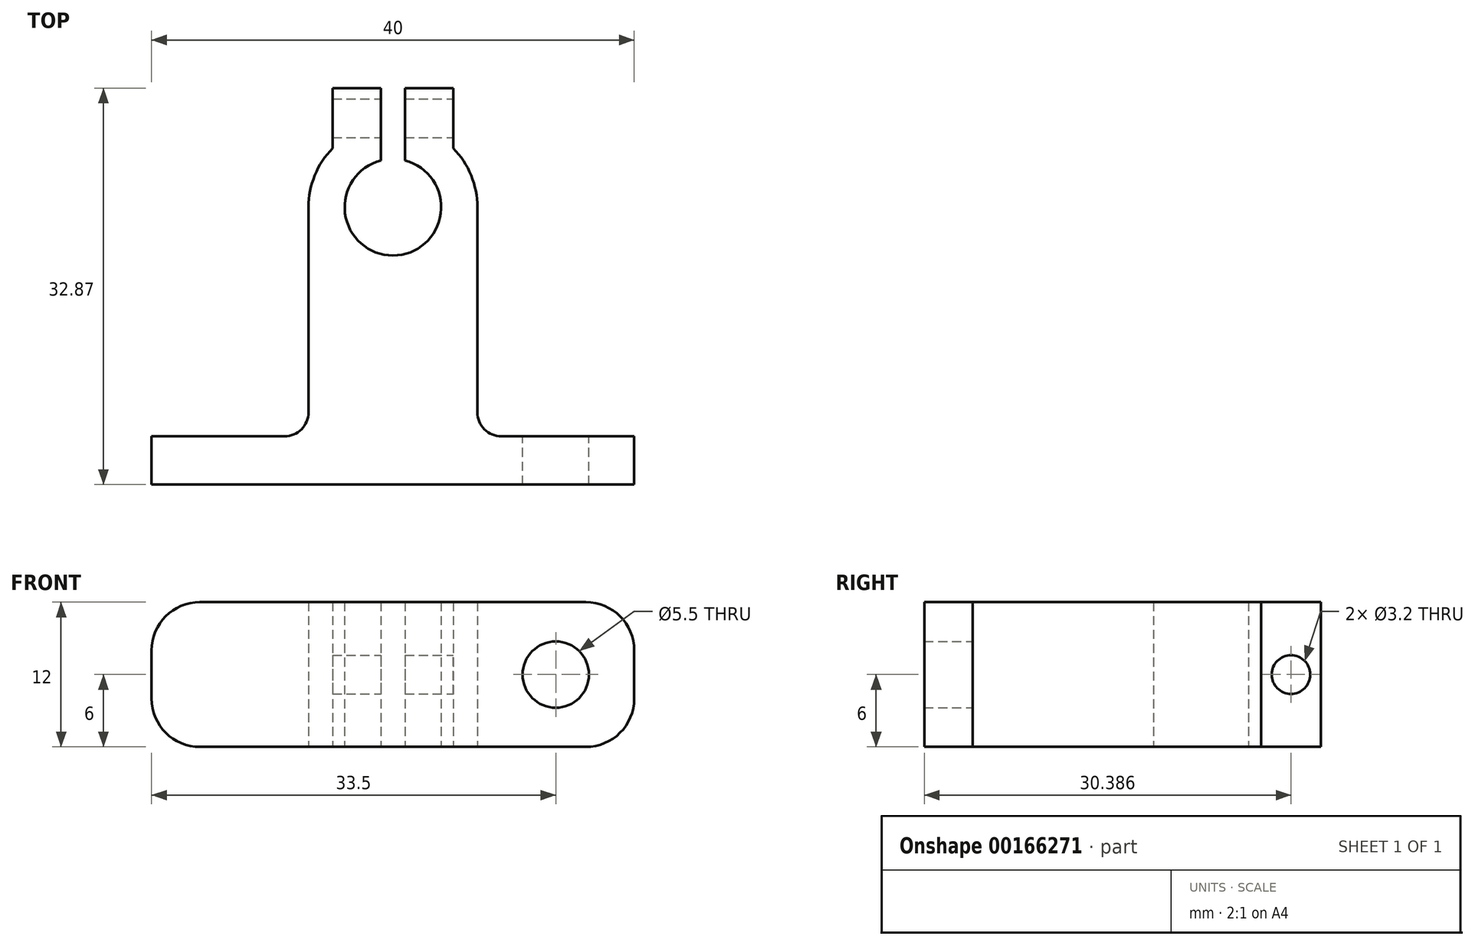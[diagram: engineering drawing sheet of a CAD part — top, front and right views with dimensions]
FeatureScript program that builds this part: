
annotation { "Feature Type Name" : "Feature", "Feature Type Description" : "" }
export const myFeature = defineFeature(function(context is Context, id is Id, definition is map)
    precondition{}
    {
        {
            var Q0;
            Q0=qCreatedBy(makeId("Top.planeOp"),FACE);
            var sketch = newSketch(context, id + "F0", { "sketchPlane" : qUnion([Q0])});
            skArc(sketch, "E0", {"start": v(-1, 3.87) * mm, "mid": v(0, -4) * mm, "end": v(1, 3.87) * mm});
            skArc(sketch, "E1.0", {"start": v(-5, 4.9) * mm, "mid": v(-6.48, 2.65) * mm, "end": v(-7, 0) * mm});
            skLineSegment(sketch, "E2", {"start": v(7, 0) * mm, "end": v(7, -19) * mm});
            skLineSegment(sketch, "E3", {"start": v(7, -19) * mm, "end": v(20, -19) * mm});
            skLineSegment(sketch, "E4", {"start": v(20, -19) * mm, "end": v(20, -23) * mm});
            skLineSegment(sketch, "E5", {"start": v(20, -23) * mm, "end": v(0, -23) * mm});
            skLineSegment(sketch, "E6", {"start": v(0, 0) * mm, "end": v(0, -23) * mm, "construction": true});
            skLineSegment(sketch, "E7", {"start": v(0, 0) * mm, "end": v(0, 4) * mm, "construction": true});
            skLineSegment(sketch, "E8.0", {"start": v(1, 3.87) * mm, "end": v(1, 6.87) * mm});
            skLineSegment(sketch, "E9.0", {"start": v(-1, 3.87) * mm, "end": v(-1, 6.93) * mm});
            skLineSegment(sketch, "E10.MirrorCS", {"start": v(-7, -19) * mm, "end": v(-20, -19) * mm});
            skLineSegment(sketch, "E11.MirrorCS", {"start": v(-20, -19) * mm, "end": v(-20, -23) * mm});
            skArc(sketch, "E12.MirrorCS", {"start": v(1, 3.87) * mm, "mid": v(0, -4) * mm, "end": v(-1, 3.87) * mm});
            skLineSegment(sketch, "E13.MirrorCS", {"start": v(-7, 0) * mm, "end": v(-7, -19) * mm});
            skLineSegment(sketch, "E14.MirrorCS", {"start": v(-20, -23) * mm, "end": v(0, -23) * mm});
            skLineSegment(sketch, "E15.top", {"start": v(-5, 9.87) * mm, "end": v(-1, 9.87) * mm});
            skLineSegment(sketch, "E15.left", {"start": v(-5, 4.9) * mm, "end": v(-5, 9.87) * mm});
            skLineSegment(sketch, "E15.right", {"start": v(-1, 3.87) * mm, "end": v(-1, 9.87) * mm});
            skLineSegment(sketch, "E16.MirrorCS", {"start": v(1, 3.87) * mm, "end": v(1, 9.87) * mm});
            skLineSegment(sketch, "E17.MirrorCS", {"start": v(5, 9.87) * mm, "end": v(1, 9.87) * mm});
            skLineSegment(sketch, "E18.MirrorCS", {"start": v(5, 4.9) * mm, "end": v(5, 9.87) * mm});
            skArc(sketch, "E19.MirrorCS", {"start": v(5, 4.9) * mm, "mid": v(6.48, 2.65) * mm, "end": v(7, 0) * mm});
            skSolve(sketch);
        }
        {
            var Q0;
            Q0=makeQuery(id+"F0.imprint","IMPRINT",FACE,{"disambiguationData":[TD([[makeQuery(id+"F0.imprint","IMPRINT",EDGE,{"derivedFrom":sQuery(id+"F0.wireOp",EDGE,"E1.0")}),1.0]])]});
            extrude(context, id + "F1", {"entities" : qUnion([Q0]), "depth" : 12 * mm});
        }
        {
            var Q0;
            Q0=makeQuery(id+"F1.opExtrude","SWEPT_FACE",FACE,{"disambiguationData":[OSD([sQuery(id+"F0.wireOp",EDGE,"E3")])]});
            var sketch = newSketch(context, id + "F2", { "sketchPlane" : qUnion([Q0])});
            skCircle(sketch, "E20", {"center": v(-13.5, 6) * mm, "radius": 2.75 * mm});
            skPoint(sketch, "E20.centerSnap0", {"position": v(-20, 6) * mm});
            skPoint(sketch, "E20.centerSnap1", {"position": v(-13.5, 0) * mm});
            skLineSegment(sketch, "E21", {"start": v(-20, 0) * mm, "end": v(20, 0) * mm, "construction": true});
            skLineSegment(sketch, "E22", {"start": v(0, 0) * mm, "end": v(0, 12) * mm, "construction": true});
            skPoint(sketch, "E22.endSnap0", {"position": v(0, 0) * mm});
            skCircle(sketch, "E23.MirrorC", {"center": v(13.5, 6) * mm, "radius": 2.75 * mm});
            skSolve(sketch);
        }
        {
            var Q0;
            Q0=makeQuery(id+"F2.imprint","IMPRINT",FACE,{"disambiguationData":[TD([[makeQuery(id+"F2.imprint","IMPRINT",EDGE,{"derivedFrom":sQuery(id+"F2.wireOp",EDGE,"E20")}),1.0]])]});
            var Q1;
            Q1=makeQuery(id+"F2.imprint","IMPRINT",FACE,{"disambiguationData":[TD([[makeQuery(id+"F2.imprint","IMPRINT",EDGE,{"derivedFrom":sQuery(id+"F2.wireOp",EDGE,"E23.MirrorC")}),-1.0]])]});
            extrude(context, id + "F3", {"entities" : qUnion([Q0, Q1]), "operationType" : NewBodyOperationType.REMOVE, "oppositeDirection" : true, "depth" : 25 * mm});
        }
        {
            var Q0;
            Q0=makeQuery(id+"F1.opExtrude","CAP_EDGE",EDGE,{"disambiguationData":[OSD([sQuery(id+"F0.wireOp",EDGE,"E4")])],"isStart":false});
            var Q1;
            Q1=makeQuery(id+"F1.opExtrude","CAP_EDGE",EDGE,{"disambiguationData":[OSD([sQuery(id+"F0.wireOp",EDGE,"E4")])],"isStart":true});
            var Q2;
            Q2=makeQuery(id+"F1.opExtrude","CAP_EDGE",EDGE,{"disambiguationData":[OSD([sQuery(id+"F0.wireOp",EDGE,"E11.MirrorCS")])],"isStart":true});
            var Q3;
            Q3=makeQuery(id+"F1.opExtrude","CAP_EDGE",EDGE,{"disambiguationData":[OSD([sQuery(id+"F0.wireOp",EDGE,"E11.MirrorCS")])],"isStart":false});
            fillet(context, id + "F4", {"entities" : qUnion([Q0, Q1, Q2, Q3]), "radius" : 4 * mm, "tangentPropagation" : true, "allowEdgeOverflow" : false});
        }
        {
            var Q0;
            Q0=makeQuery(id+"F1.opExtrude","SWEPT_EDGE",EDGE,{"disambiguationData":[OSD([sQuery(id+"F0.wireOp",EDGE,"E2"),sQuery(id+"F0.wireOp",EDGE,"E3")])]});
            var Q1;
            Q1=makeQuery(id+"F1.opExtrude","SWEPT_EDGE",EDGE,{"disambiguationData":[OSD([sQuery(id+"F0.wireOp",EDGE,"E13.MirrorCS"),sQuery(id+"F0.wireOp",EDGE,"E10.MirrorCS")])]});
            fillet(context, id + "F5", {"entities" : qUnion([Q0, Q1]), "radius" : 2 * mm, "tangentPropagation" : true, "allowEdgeOverflow" : false});
        }
        {
            var Q0;
            Q0=makeQuery(id+"F1.opExtrude","SWEPT_FACE",FACE,{"disambiguationData":[OSD([sQuery(id+"F0.wireOp",EDGE,"E18.MirrorCS")])]});
            var sketch = newSketch(context, id + "F6", { "sketchPlane" : qUnion([Q0])});
            skCircle(sketch, "E24", {"center": v(7.39, 6) * mm, "radius": 1.6 * mm});
            skPoint(sketch, "E24.centerSnap0", {"position": v(9.87, 6) * mm});
            skPoint(sketch, "E24.centerSnap1", {"position": v(7.39, 0) * mm});
            skSolve(sketch);
        }
        {
            var Q0;
            Q0=makeQuery(id+"F6.imprint","IMPRINT",FACE,{"disambiguationData":[TD([[makeQuery(id+"F6.imprint","IMPRINT",EDGE,{"derivedFrom":sQuery(id+"F6.wireOp",EDGE,"E24")}),1.0]])]});
            extrude(context, id + "F7", {"entities" : qUnion([Q0]), "operationType" : NewBodyOperationType.REMOVE, "endBound" : BoundingType.THROUGH_ALL, "oppositeDirection" : true, "depth" : 25 * mm});
        }
    });
